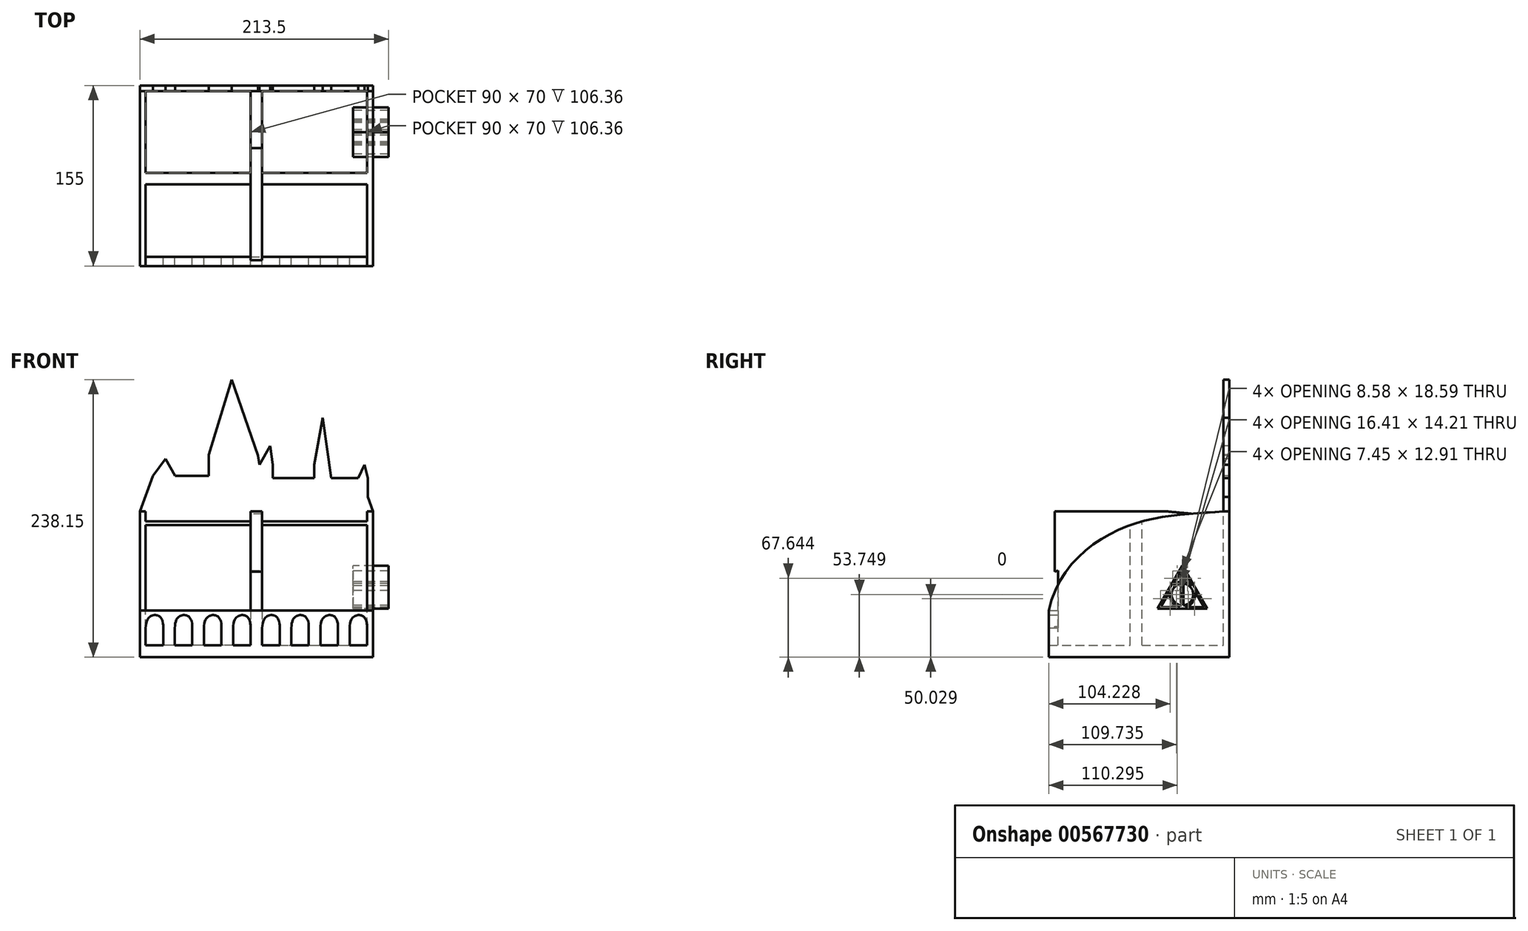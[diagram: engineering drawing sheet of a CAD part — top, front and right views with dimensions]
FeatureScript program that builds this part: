
annotation { "Feature Type Name" : "Feature", "Feature Type Description" : "" }
export const myFeature = defineFeature(function(context is Context, id is Id, definition is map)
    precondition{}
    {
        {
            var Q0;
            Q0=qCreatedBy(makeId("Front.planeOp"),FACE);
            var sketch = newSketch(context, id + "F0", { "sketchPlane" : qUnion([Q0])});
            skLineSegment(sketch, "E0", {"start": v(-120, -65.8) * mm, "end": v(80, -65.8) * mm});
            skLineSegment(sketch, "E1", {"start": v(-120, -65.8) * mm, "end": v(-120, -25.8) * mm});
            skLineSegment(sketch, "E2", {"start": v(80, -65.8) * mm, "end": v(80, -25.8) * mm});
            skLineSegment(sketch, "E3", {"start": v(-120, -25.8) * mm, "end": v(80, -25.8) * mm});
            skLineSegment(sketch, "E4", {"start": v(-115, -55.8) * mm, "end": v(-100, -55.8) * mm});
            skLineSegment(sketch, "E5", {"start": v(-90, -55.8) * mm, "end": v(-75, -55.8) * mm});
            skLineSegment(sketch, "E6", {"start": v(-65, -55.8) * mm, "end": v(-50, -55.8) * mm});
            skLineSegment(sketch, "E7", {"start": v(-40, -55.8) * mm, "end": v(-25, -55.8) * mm});
            skLineSegment(sketch, "E8", {"start": v(-15, -55.8) * mm, "end": v(0, -55.8) * mm});
            skLineSegment(sketch, "E9", {"start": v(10, -55.8) * mm, "end": v(25, -55.8) * mm});
            skLineSegment(sketch, "E10", {"start": v(35, -55.8) * mm, "end": v(50, -55.8) * mm});
            skLineSegment(sketch, "E11", {"start": v(60, -55.8) * mm, "end": v(75, -55.8) * mm});
            skLineSegment(sketch, "E12", {"start": v(-115, -55.8) * mm, "end": v(-115, -40.8) * mm});
            skLineSegment(sketch, "E13", {"start": v(-100, -55.8) * mm, "end": v(-100, -40.8) * mm});
            skLineSegment(sketch, "E14", {"start": v(-90, -55.8) * mm, "end": v(-90, -40.8) * mm});
            skLineSegment(sketch, "E15", {"start": v(-75, -55.8) * mm, "end": v(-75, -40.8) * mm});
            skLineSegment(sketch, "E16", {"start": v(-65, -55.8) * mm, "end": v(-65, -40.8) * mm});
            skLineSegment(sketch, "E17", {"start": v(-50, -55.8) * mm, "end": v(-50, -40.8) * mm});
            skLineSegment(sketch, "E18", {"start": v(-40, -55.8) * mm, "end": v(-40, -40.8) * mm});
            skLineSegment(sketch, "E19", {"start": v(-25, -55.8) * mm, "end": v(-25, -40.8) * mm});
            skLineSegment(sketch, "E20", {"start": v(-15, -55.8) * mm, "end": v(-15, -40.8) * mm});
            skLineSegment(sketch, "E21", {"start": v(0, -55.8) * mm, "end": v(0, -40.8) * mm});
            skLineSegment(sketch, "E22", {"start": v(10, -55.8) * mm, "end": v(10, -40.8) * mm});
            skLineSegment(sketch, "E23", {"start": v(25, -55.8) * mm, "end": v(25, -40.8) * mm});
            skLineSegment(sketch, "E24", {"start": v(35, -55.8) * mm, "end": v(35, -40.8) * mm});
            skLineSegment(sketch, "E25", {"start": v(50, -55.8) * mm, "end": v(50, -40.8) * mm});
            skLineSegment(sketch, "E26", {"start": v(60, -55.8) * mm, "end": v(60, -40.8) * mm});
            skLineSegment(sketch, "E27", {"start": v(75, -55.8) * mm, "end": v(75, -40.8) * mm});
            skFitSpline(sketch, "E28", {"points": [v(-115, -40.8) * mm, v(-107.07, -29.73) * mm, v(-100, -40.8) * mm], "startDerivative": vector(0.6, 51.8) * mm, "endDerivative": vector(-1.33, -52.67) * mm});
            skFitSpline(sketch, "E29", {"points": [v(-90, -40.8) * mm, v(-82.07, -29.73) * mm, v(-75, -40.8) * mm], "startDerivative": vector(0.6, 51.8) * mm, "endDerivative": vector(-1.33, -52.67) * mm});
            skFitSpline(sketch, "E30", {"points": [v(-65, -40.8) * mm, v(-57.07, -29.73) * mm, v(-50, -40.8) * mm], "startDerivative": vector(0.6, 51.8) * mm, "endDerivative": vector(-1.33, -52.67) * mm});
            skFitSpline(sketch, "E31", {"points": [v(-40, -40.8) * mm, v(-32.07, -29.73) * mm, v(-25, -40.8) * mm], "startDerivative": vector(0.6, 51.8) * mm, "endDerivative": vector(-1.33, -52.67) * mm});
            skFitSpline(sketch, "E32", {"points": [v(-15, -40.8) * mm, v(-7.07, -29.73) * mm, v(0, -40.8) * mm], "startDerivative": vector(0.6, 51.8) * mm, "endDerivative": vector(-1.33, -52.67) * mm});
            skFitSpline(sketch, "E33", {"points": [v(10, -40.8) * mm, v(17.93, -29.73) * mm, v(25, -40.8) * mm], "startDerivative": vector(0.6, 51.8) * mm, "endDerivative": vector(-1.33, -52.67) * mm});
            skFitSpline(sketch, "E34", {"points": [v(35, -40.8) * mm, v(42.93, -29.73) * mm, v(50, -40.8) * mm], "startDerivative": vector(0.6, 51.8) * mm, "endDerivative": vector(-1.33, -52.67) * mm});
            skFitSpline(sketch, "E35", {"points": [v(60, -40.8) * mm, v(67.93, -29.73) * mm, v(75, -40.8) * mm], "startDerivative": vector(0.6, 51.8) * mm, "endDerivative": vector(-1.33, -52.67) * mm});
            skSolve(sketch);
        }
        {
            var Q0;
            Q0=makeQuery(id+"F0.imprint","IMPRINT",FACE,{"disambiguationData":[TD([[makeQuery(id+"F0.imprint","IMPRINT",EDGE,{"derivedFrom":sQuery(id+"F0.wireOp",EDGE,"E0")}),1.0]])]});
            extrude(context, id + "F1", {"entities" : qUnion([Q0]), "depth" : 8 * mm, "offsetDistance" : 25 * mm});
        }
        {
            var Q0;
            Q0=makeQuery(id+"F1.opExtrude","SWEPT_FACE",FACE,{"disambiguationData":[OSD([sQuery(id+"F0.wireOp",EDGE,"E2")])]});
            var sketch = newSketch(context, id + "F2", { "sketchPlane" : qUnion([Q0])});
            skLineSegment(sketch, "E36", {"start": v(-8, -65.8) * mm, "end": v(142, -65.8) * mm});
            skLineSegment(sketch, "E37", {"start": v(142, -65.8) * mm, "end": v(142, 59.2) * mm});
            skFitSpline(sketch, "E38", {"points": [v(142, 59.2) * mm, v(58.95, 46.28) * mm, v(-8, -25.8) * mm], "startDerivative": vector(-167.04, -11.97) * mm, "endDerivative": vector(-46.18, -213.97) * mm});
            skSolve(sketch);
        }
        {
            var Q0;
            Q0=makeQuery(id+"F1.opExtrude","CAP_FACE",FACE,{"disambiguationData":[OSD([sQuery(id+"F0.wireOp",EDGE,"E0"),sQuery(id+"F0.wireOp",EDGE,"E1"),sQuery(id+"F0.wireOp",EDGE,"E2"),sQuery(id+"F0.wireOp",EDGE,"E3"),sQuery(id+"F0.wireOp",EDGE,"E4"),sQuery(id+"F0.wireOp",EDGE,"E5"),sQuery(id+"F0.wireOp",EDGE,"E6"),sQuery(id+"F0.wireOp",EDGE,"E7"),sQuery(id+"F0.wireOp",EDGE,"E8"),sQuery(id+"F0.wireOp",EDGE,"E9"),sQuery(id+"F0.wireOp",EDGE,"E10"),sQuery(id+"F0.wireOp",EDGE,"E11"),sQuery(id+"F0.wireOp",EDGE,"E12"),sQuery(id+"F0.wireOp",EDGE,"E13"),sQuery(id+"F0.wireOp",EDGE,"E14"),sQuery(id+"F0.wireOp",EDGE,"E15"),sQuery(id+"F0.wireOp",EDGE,"E16"),sQuery(id+"F0.wireOp",EDGE,"E17"),sQuery(id+"F0.wireOp",EDGE,"E18"),sQuery(id+"F0.wireOp",EDGE,"E19"),sQuery(id+"F0.wireOp",EDGE,"E20"),sQuery(id+"F0.wireOp",EDGE,"E21"),sQuery(id+"F0.wireOp",EDGE,"E22"),sQuery(id+"F0.wireOp",EDGE,"E23"),sQuery(id+"F0.wireOp",EDGE,"E24"),sQuery(id+"F0.wireOp",EDGE,"E25"),sQuery(id+"F0.wireOp",EDGE,"E26"),sQuery(id+"F0.wireOp",EDGE,"E27"),sQuery(id+"F0.wireOp",EDGE,"E28"),sQuery(id+"F0.wireOp",EDGE,"E29"),sQuery(id+"F0.wireOp",EDGE,"E30"),sQuery(id+"F0.wireOp",EDGE,"E31"),sQuery(id+"F0.wireOp",EDGE,"E32"),sQuery(id+"F0.wireOp",EDGE,"E33"),sQuery(id+"F0.wireOp",EDGE,"E34"),sQuery(id+"F0.wireOp",EDGE,"E35")])],"isStart":true});
            cPlane(context, id + "F3", {"entities" : qUnion([Q0]), "cplaneType" : CPlaneType.OFFSET, "offset" : 142 * mm, "width" : 150 * mm, "height" : 150 * mm});
        }
        {
            var Q0;
            Q0=qCreatedBy(id+"F3.planeOp",FACE);
            var sketch = newSketch(context, id + "F4", { "sketchPlane" : qUnion([Q0])});
            skPoint(sketch, "E39.0", {"position": v(-80, 59.2) * mm});
            skPoint(sketch, "E40.0", {"position": v(-80, -65.8) * mm});
            skPoint(sketch, "E41", {"position": v(120, 59.2) * mm});
            skPoint(sketch, "E42", {"position": v(120, -65.8) * mm});
            skLineSegment(sketch, "E43", {"start": v(-80, 59.2) * mm, "end": v(-80, -65.8) * mm});
            skLineSegment(sketch, "E44", {"start": v(-80, -65.8) * mm, "end": v(120, -65.8) * mm});
            skLineSegment(sketch, "E45", {"start": v(120, -65.8) * mm, "end": v(120, 59.2) * mm});
            skLineSegment(sketch, "E46", {"start": v(-80, 59.2) * mm, "end": v(-75.6, 71.64) * mm});
            skLineSegment(sketch, "E47", {"start": v(-75.6, 71.64) * mm, "end": v(-75.6, 87.92) * mm});
            skLineSegment(sketch, "E48", {"start": v(-75.6, 87.92) * mm, "end": v(-72.68, 99.19) * mm});
            skLineSegment(sketch, "E49", {"start": v(-72.68, 99.19) * mm, "end": v(-67.26, 87.92) * mm});
            skLineSegment(sketch, "E50", {"start": v(-67.26, 87.92) * mm, "end": v(-44.24, 87.92) * mm});
            skLineSegment(sketch, "E51", {"start": v(-44.24, 87.92) * mm, "end": v(-36.93, 139.5) * mm});
            skLineSegment(sketch, "E52", {"start": v(-36.93, 139.5) * mm, "end": v(-29.61, 99.19) * mm});
            skLineSegment(sketch, "E53", {"start": v(-29.61, 99.19) * mm, "end": v(-29.61, 87.92) * mm});
            skLineSegment(sketch, "E54", {"start": v(-29.61, 87.92) * mm, "end": v(5.9, 87.92) * mm});
            skLineSegment(sketch, "E55", {"start": v(5.9, 87.92) * mm, "end": v(5.9, 99.19) * mm});
            skLineSegment(sketch, "E56", {"start": v(5.9, 99.19) * mm, "end": v(8.21, 115.44) * mm});
            skLineSegment(sketch, "E57", {"start": v(8.21, 115.44) * mm, "end": v(17.42, 99.19) * mm});
            skLineSegment(sketch, "E58", {"start": v(17.42, 99.19) * mm, "end": v(18.57, 107.31) * mm});
            skPoint(sketch, "E58.endSnap0", {"position": v(12.82, 107.31) * mm});
            skLineSegment(sketch, "E59", {"start": v(18.57, 107.31) * mm, "end": v(41.03, 172.35) * mm});
            skLineSegment(sketch, "E60", {"start": v(41.03, 172.35) * mm, "end": v(60.84, 107.7) * mm});
            skLineSegment(sketch, "E61", {"start": v(60.84, 107.7) * mm, "end": v(60.84, 89.66) * mm});
            skLineSegment(sketch, "E62", {"start": v(60.84, 89.66) * mm, "end": v(89.78, 89.66) * mm});
            skLineSegment(sketch, "E63", {"start": v(89.78, 89.66) * mm, "end": v(98.17, 104.34) * mm});
            skLineSegment(sketch, "E64", {"start": v(98.17, 104.34) * mm, "end": v(108.65, 89.66) * mm});
            skLineSegment(sketch, "E65", {"start": v(108.65, 89.66) * mm, "end": v(120, 59.2) * mm});
            skSolve(sketch);
        }
        {
            var Q0;
            Q0=makeQuery(id+"F1.opExtrude","SWEPT_FACE",FACE,{"disambiguationData":[OSD([sQuery(id+"F0.wireOp",EDGE,"E1")])]});
            var sketch = newSketch(context, id + "F5", { "sketchPlane" : qUnion([Q0])});
            skPoint(sketch, "E66.0", {"position": v(-142, 59.2) * mm});
            skPoint(sketch, "E67.0", {"position": v(-142, -65.8) * mm});
            skLineSegment(sketch, "E68", {"start": v(-142, 59.2) * mm, "end": v(-142, -65.8) * mm});
            skLineSegment(sketch, "E69", {"start": v(-142, -65.8) * mm, "end": v(0, -65.8) * mm});
            skLineSegment(sketch, "E70", {"start": v(0, -65.8) * mm, "end": v(0, -25.8) * mm});
            skLineSegment(sketch, "E71", {"start": v(0, -25.8) * mm, "end": v(8, -25.8) * mm});
            skFitSpline(sketch, "E72.MirrorCS", {"points": [v(-142, 59.2) * mm, v(-58.95, 46.28) * mm, v(8, -25.8) * mm], "startDerivative": vector(167.04, -11.97) * mm, "endDerivative": vector(46.18, -213.97) * mm});
            skSolve(sketch);
        }
        {
            var Q0;
            Q0=makeQuery(id+"F1.opExtrude","SWEPT_FACE",FACE,{"disambiguationData":[OSD([sQuery(id+"F0.wireOp",EDGE,"E0")])]});
            var sketch = newSketch(context, id + "F6", { "sketchPlane" : qUnion([Q0])});
            skPoint(sketch, "E73.0", {"position": v(-120, 8) * mm});
            skPoint(sketch, "E74.0", {"position": v(-120, -142) * mm});
            skPoint(sketch, "E75.0", {"position": v(80, -142) * mm});
            skPoint(sketch, "E76.0", {"position": v(80, 8) * mm});
            skLineSegment(sketch, "E77.bottom", {"start": v(-120, 8) * mm, "end": v(80, 8) * mm});
            skLineSegment(sketch, "E77.top", {"start": v(-120, -142) * mm, "end": v(80, -142) * mm});
            skLineSegment(sketch, "E77.left", {"start": v(-120, 8) * mm, "end": v(-120, -142) * mm});
            skLineSegment(sketch, "E77.right", {"start": v(80, 8) * mm, "end": v(80, -142) * mm});
            skSolve(sketch);
        }
        {
            var Q0;
            {var subQ0=sQuery(id+"F6.wireOp",EDGE,"E77.top");Q0=makeQuery(id+"F6.imprint","IMPRINT",FACE,{"disambiguationData":[TD([[makeQuery(id+"F6.imprint","IMPRINT",EDGE,{"derivedFrom":subQ0}),1.0]])]});}
            extrude(context, id + "F7", {"entities" : qUnion([Q0]), "operationType" : NewBodyOperationType.ADD, "oppositeDirection" : true, "depth" : 10 * mm, "offsetDistance" : 25 * mm});
        }
        {
            var Q0;
            {var subQ1=sQuery(id+"F2.wireOp",EDGE,"E37");Q0=makeQuery(id+"F2.imprint","IMPRINT",FACE,{"disambiguationData":[TD([[makeQuery(id+"F2.imprint","IMPRINT",EDGE,{"derivedFrom":subQ1}),1.0]])]});}
            extrude(context, id + "F8", {"entities" : qUnion([Q0]), "operationType" : NewBodyOperationType.ADD, "oppositeDirection" : true, "depth" : 5 * mm, "offsetDistance" : 25 * mm});
        }
        {
            var Q0;
            Q0=makeQuery(id+"F5.imprint","IMPRINT",FACE,{"disambiguationData":[TD([[makeQuery(id+"F5.imprint","IMPRINT",EDGE,{"derivedFrom":sQuery(id+"F5.wireOp",EDGE,"E68")}),1.0]])]});
            extrude(context, id + "F9", {"entities" : qUnion([Q0]), "operationType" : NewBodyOperationType.ADD, "oppositeDirection" : true, "depth" : 5 * mm, "offsetDistance" : 25 * mm});
        }
        {
            var Q0;
            Q0=makeQuery(id+"F4.imprint","IMPRINT",FACE,{"disambiguationData":[TD([[makeQuery(id+"F4.imprint","IMPRINT",EDGE,{"derivedFrom":sQuery(id+"F4.wireOp",EDGE,"E43")}),1.0]])]});
            extrude(context, id + "F10", {"entities" : qUnion([Q0]), "operationType" : NewBodyOperationType.ADD, "depth" : 5 * mm, "offsetDistance" : 25 * mm});
        }
        {
            var Q0;
            Q0=makeQuery(id+"F10.opExtrude","CAP_FACE",FACE,{"disambiguationData":[OSD([sQuery(id+"F4.wireOp",EDGE,"E43"),sQuery(id+"F4.wireOp",EDGE,"E44"),sQuery(id+"F4.wireOp",EDGE,"E45"),sQuery(id+"F4.wireOp",EDGE,"E46"),sQuery(id+"F4.wireOp",EDGE,"E47"),sQuery(id+"F4.wireOp",EDGE,"E48"),sQuery(id+"F4.wireOp",EDGE,"E49"),sQuery(id+"F4.wireOp",EDGE,"E50"),sQuery(id+"F4.wireOp",EDGE,"E51"),sQuery(id+"F4.wireOp",EDGE,"E52"),sQuery(id+"F4.wireOp",EDGE,"E53"),sQuery(id+"F4.wireOp",EDGE,"E54"),sQuery(id+"F4.wireOp",EDGE,"E55"),sQuery(id+"F4.wireOp",EDGE,"E56"),sQuery(id+"F4.wireOp",EDGE,"E57"),sQuery(id+"F4.wireOp",EDGE,"E58"),sQuery(id+"F4.wireOp",EDGE,"E59"),sQuery(id+"F4.wireOp",EDGE,"E60"),sQuery(id+"F4.wireOp",EDGE,"E61"),sQuery(id+"F4.wireOp",EDGE,"E62"),sQuery(id+"F4.wireOp",EDGE,"E63"),sQuery(id+"F4.wireOp",EDGE,"E64"),sQuery(id+"F4.wireOp",EDGE,"E65")])],"isStart":true});
            var sketch = newSketch(context, id + "F11", { "sketchPlane" : qUnion([Q0])});
            skLineSegment(sketch, "E78", {"start": v(-115, -55.8) * mm, "end": v(-25, -55.8) * mm});
            skLineSegment(sketch, "E79.bottom", {"start": v(-25, -55.8) * mm, "end": v(-15, -55.8) * mm});
            skLineSegment(sketch, "E79.top", {"start": v(-25, 59.2) * mm, "end": v(-15, 59.2) * mm});
            skLineSegment(sketch, "E79.left", {"start": v(-25, -55.8) * mm, "end": v(-25, 59.2) * mm});
            skLineSegment(sketch, "E79.right", {"start": v(-15, -55.8) * mm, "end": v(-15, 59.2) * mm});
            skSolve(sketch);
        }
        {
            var Q0;
            Q0=makeQuery(id+"F9.boolean.opBoolean","MERGE",FACE,{"derivedFrom":[makeQuery(id+"F1.opExtrude","SWEPT_FACE",FACE,{"disambiguationData":[OSD([sQuery(id+"F0.wireOp",EDGE,"E12")])]}),makeQuery(id+"F9.opExtrude","CAP_FACE",FACE,{"disambiguationData":[OSD([sQuery(id+"F5.wireOp",EDGE,"E68"),sQuery(id+"F5.wireOp",EDGE,"E69"),sQuery(id+"F5.wireOp",EDGE,"E70"),sQuery(id+"F5.wireOp",EDGE,"E71"),sQuery(id+"F5.wireOp",EDGE,"E72.MirrorCS")])],"isStart":false})]});
            var sketch = newSketch(context, id + "F12", { "sketchPlane" : qUnion([Q0])});
            skLineSegment(sketch, "E80", {"start": v(-8, -55.8) * mm, "end": v(62, -55.8) * mm});
            skLineSegment(sketch, "E81.bottom", {"start": v(62, -55.8) * mm, "end": v(72, -55.8) * mm});
            skLineSegment(sketch, "E81.top", {"start": v(62, 90.16) * mm, "end": v(72, 90.16) * mm});
            skLineSegment(sketch, "E81.left", {"start": v(62, -55.8) * mm, "end": v(62, 90.16) * mm});
            skLineSegment(sketch, "E81.right", {"start": v(72, -55.8) * mm, "end": v(72, 90.16) * mm});
            skSolve(sketch);
        }
        {
            var Q0;
            {var subQ0=sQuery(id+"F12.wireOp",EDGE,"E81.bottom");Q0=makeQuery(id+"F12.imprint","IMPRINT",FACE,{"disambiguationData":[TD([[makeQuery(id+"F12.imprint","IMPRINT",EDGE,{"derivedFrom":subQ0}),1.0]])]});}
            extrude(context, id + "F13", {"entities" : qUnion([Q0]), "operationType" : NewBodyOperationType.ADD, "depth" : 90 * mm, "offsetDistance" : 25 * mm});
        }
        {
            var Q0;
            Q0=makeQuery(id+"F8.boolean.opBoolean","MERGE",FACE,{"derivedFrom":[makeQuery(id+"F1.opExtrude","SWEPT_FACE",FACE,{"disambiguationData":[OSD([sQuery(id+"F0.wireOp",EDGE,"E27")])]}),makeQuery(id+"F8.opExtrude","CAP_FACE",FACE,{"disambiguationData":[OSD([sQuery(id+"F0.wireOp",EDGE,"E2"),sQuery(id+"F0.wireOp",EDGE,"E3"),sQuery(id+"F2.wireOp",EDGE,"E36"),sQuery(id+"F2.wireOp",EDGE,"E37"),sQuery(id+"F2.wireOp",EDGE,"E38")])],"isStart":false})]});
            var sketch = newSketch(context, id + "F14", { "sketchPlane" : qUnion([Q0])});
            skLineSegment(sketch, "E82", {"start": v(-142, -55.8) * mm, "end": v(-72, -55.8) * mm});
            skLineSegment(sketch, "E83.bottom", {"start": v(-72, -55.8) * mm, "end": v(-62, -55.8) * mm});
            skLineSegment(sketch, "E83.top", {"start": v(-72, 77.76) * mm, "end": v(-62, 77.76) * mm});
            skLineSegment(sketch, "E83.left", {"start": v(-72, -55.8) * mm, "end": v(-72, 77.76) * mm});
            skLineSegment(sketch, "E83.right", {"start": v(-62, -55.8) * mm, "end": v(-62, 77.76) * mm});
            skSolve(sketch);
        }
        {
            var Q0;
            {var subQ0=sQuery(id+"F14.wireOp",EDGE,"E83.bottom");Q0=makeQuery(id+"F14.imprint","IMPRINT",FACE,{"disambiguationData":[TD([[makeQuery(id+"F14.imprint","IMPRINT",EDGE,{"derivedFrom":subQ0}),-1.0]])]});}
            extrude(context, id + "F15", {"entities" : qUnion([Q0]), "operationType" : NewBodyOperationType.ADD, "depth" : 90 * mm, "offsetDistance" : 25 * mm});
        }
        {
            var Q0;
            Q0=makeQuery(id+"F11.imprint","IMPRINT",FACE,{"disambiguationData":[TD([[makeQuery(id+"F11.imprint","IMPRINT",EDGE,{"derivedFrom":sQuery(id+"F11.wireOp",EDGE,"E79.bottom")}),1.0]])]});
            extrude(context, id + "F16", {"entities" : qUnion([Q0]), "operationType" : NewBodyOperationType.ADD, "depth" : 145 * mm, "offsetDistance" : 25 * mm});
        }
        {
            var Q0;
            Q0=makeQuery(id+"F16.boolean.opBoolean","MERGE",FACE,{"derivedFrom":[makeQuery(id+"F1.opExtrude","SWEPT_FACE",FACE,{"disambiguationData":[OSD([sQuery(id+"F0.wireOp",EDGE,"E20")])]}),makeQuery(id+"F16.opExtrude","SWEPT_FACE",FACE,{"disambiguationData":[OSD([sQuery(id+"F11.wireOp",EDGE,"E79.right")])]})]});
            var sketch = newSketch(context, id + "F17", { "sketchPlane" : qUnion([Q0])});
            skFitSpline(sketch, "E84.0", {"points": [v(142, 59.2) * mm, v(115.26, 57.28) * mm, v(55.74, 56.51) * mm, v(0, 11.26) * mm, v(-8, -25.8) * mm]});
            skLineSegment(sketch, "E85.0", {"start": v(-3, 59.2) * mm, "end": v(142, 59.2) * mm});
            skLineSegment(sketch, "E86", {"start": v(-3, 59.2) * mm, "end": v(-3, -9.9) * mm});
            skSolve(sketch);
        }
        {
            var Q0;
            {var subQ0=sQuery(id+"F17.wireOp",EDGE,"E85.0");Q0=makeQuery(id+"F17.imprint","IMPRINT",FACE,{"disambiguationData":[TD([[makeQuery(id+"F17.imprint","IMPRINT",EDGE,{"derivedFrom":subQ0}),-1.0]])]});}
            extrude(context, id + "F18", {"entities" : qUnion([Q0]), "operationType" : NewBodyOperationType.REMOVE, "oppositeDirection" : true, "depth" : 51 * mm, "offsetDistance" : 25 * mm});
        }
        {
            var Q0;
            {var subQ22=sQuery(id+"F0.wireOp",EDGE,"E20");var subQ33=sQuery(id+"F0.wireOp",EDGE,"E3");var subQ37=sQuery(id+"F11.wireOp",EDGE,"E79.right");Q0=makeQuery(id+"F18.boolean.opBoolean","SPLIT",FACE,{"disambiguationData":[TD([makeQuery(id+"F1.opExtrude","SWEPT_FACE",FACE,{"disambiguationData":[OSD([subQ33])]})])],"derivedFrom":makeQuery(id+"F16.boolean.opBoolean","MERGE",FACE,{"derivedFrom":[makeQuery(id+"F1.opExtrude","SWEPT_FACE",FACE,{"disambiguationData":[OSD([subQ22])]}),makeQuery(id+"F16.opExtrude","SWEPT_FACE",FACE,{"disambiguationData":[OSD([subQ37])]})]})});}
            var sketch = newSketch(context, id + "F19", { "sketchPlane" : qUnion([Q0])});
            skLineSegment(sketch, "E87", {"start": v(0, -25.8) * mm, "end": v(-3, -25.8) * mm});
            skLineSegment(sketch, "E88", {"start": v(-3, -25.8) * mm, "end": v(-3, -9.9) * mm});
            skLineSegment(sketch, "E89", {"start": v(0, -25.8) * mm, "end": v(0, 8.53) * mm});
            skLineSegment(sketch, "E90", {"start": v(0, 8.53) * mm, "end": v(-3, 7.58) * mm});
            skLineSegment(sketch, "E91", {"start": v(-3, 7.58) * mm, "end": v(-3, -9.9) * mm});
            skSolve(sketch);
        }
        {
            var Q0;
            {var subQ0=sQuery(id+"F19.wireOp",EDGE,"E87");Q0=makeQuery(id+"F19.imprint","IMPRINT",FACE,{"disambiguationData":[TD([[makeQuery(id+"F19.imprint","IMPRINT",EDGE,{"derivedFrom":subQ0}),-1.0]])]});}
            extrude(context, id + "F20", {"entities" : qUnion([Q0]), "operationType" : NewBodyOperationType.REMOVE, "oppositeDirection" : true, "depth" : 25 * mm, "offsetDistance" : 25 * mm});
        }
        {
            var Q0;
            {var subQ0=sQuery(id+"F0.wireOp",EDGE,"E2");Q0=makeQuery(id+"F10.boolean.opBoolean","MERGE",FACE,{"derivedFrom":[makeQuery(id+"F8.boolean.opBoolean","MERGE",FACE,{"derivedFrom":[makeQuery(id+"F7.boolean.opBoolean","MERGE",FACE,{"derivedFrom":[makeQuery(id+"F1.opExtrude","SWEPT_FACE",FACE,{"disambiguationData":[OSD([subQ0])]}),makeQuery(id+"F7.opExtrude","SWEPT_FACE",FACE,{"disambiguationData":[OSD([sQuery(id+"F6.wireOp",EDGE,"E77.right")])]})]}),makeQuery(id+"F8.opExtrude","CAP_FACE",FACE,{"disambiguationData":[OSD([subQ0,sQuery(id+"F0.wireOp",EDGE,"E3"),sQuery(id+"F2.wireOp",EDGE,"E36"),sQuery(id+"F2.wireOp",EDGE,"E37"),sQuery(id+"F2.wireOp",EDGE,"E38")])],"isStart":true})]}),makeQuery(id+"F10.opExtrude","SWEPT_FACE",FACE,{"disambiguationData":[OSD([sQuery(id+"F4.wireOp",EDGE,"E43")])]})]});}
            cPlane(context, id + "F21", {"entities" : qUnion([Q0]), "cplaneType" : CPlaneType.OFFSET, "offset" : 0 * mm, "width" : 150 * mm, "height" : 150 * mm});
        }
        {
            var Q0;
            Q0=qCreatedBy(id+"F21.planeOp",FACE);
            var sketch = newSketch(context, id + "F22", { "sketchPlane" : qUnion([Q0])});
            skLineSegment(sketch, "E92", {"start": v(28.04, -45.75) * mm, "end": v(44.45, -17.33) * mm});
            skLineSegment(sketch, "E93", {"start": v(67.04, 16.6) * mm, "end": v(81.95, -9.22) * mm});
            skLineSegment(sketch, "E94", {"start": v(28.04, -45.75) * mm, "end": v(60.86, -45.75) * mm});
            skPoint(sketch, "E95.0", {"position": v(69.5, -65.8) * mm});
            skLineSegment(sketch, "E96.0", {"start": v(22.85, -48.75) * mm, "end": v(65.54, 25.2) * mm});
            skLineSegment(sketch, "E96.1", {"start": v(22.85, -48.75) * mm, "end": v(108.24, -48.75) * mm});
            skLineSegment(sketch, "E96.2", {"start": v(65.54, 25.2) * mm, "end": v(108.24, -48.75) * mm});
            skLineSegment(sketch, "E97.left", {"start": v(64.04, 16.6) * mm, "end": v(64.04, -2) * mm});
            skLineSegment(sketch, "E97.right", {"start": v(67.04, 16.6) * mm, "end": v(67.04, -2) * mm});
            skPoint(sketch, "E97.middle", {"position": v(65.54, -13.28) * mm});
            skArc(sketch, "E98.0", {"start": v(64.04, -5.51) * mm, "mid": v(46.9, -24.1) * mm, "end": v(64.04, -42.7) * mm});
            skLineSegment(sketch, "E99.trimOffspring", {"start": v(64.04, -5.51) * mm, "end": v(64.04, -42.7) * mm});
            skLineSegment(sketch, "E100.trimOffspring", {"start": v(67.04, -5.51) * mm, "end": v(67.04, -42.7) * mm});
            skPoint(sketch, "E101.orphan", {"position": v(64.04, 19.2) * mm});
            skPoint(sketch, "E102.orphan", {"position": v(67.04, 19.2) * mm});
            skPoint(sketch, "E103.orphan", {"position": v(65.54, 19.2) * mm});
            skArc(sketch, "E104.trimOffspring", {"start": v(67.04, -42.7) * mm, "mid": v(84.2, -24.1) * mm, "end": v(67.04, -5.51) * mm});
            skLineSegment(sketch, "E105.trimOffspring", {"start": v(70.22, -45.75) * mm, "end": v(103.04, -45.75) * mm});
            skLineSegment(sketch, "E106.trimOffspring", {"start": v(64.04, -45.7) * mm, "end": v(64.04, -45.75) * mm});
            skLineSegment(sketch, "E107.trimOffspring", {"start": v(67.04, -45.7) * mm, "end": v(67.04, -45.75) * mm});
            skArc(sketch, "E108.0", {"start": v(70.22, -45.75) * mm, "mid": v(84.73, -35.18) * mm, "end": v(86.63, -17.33) * mm});
            skArc(sketch, "E109.0", {"start": v(64.01, -2) * mm, "mid": v(55.87, -4.17) * mm, "end": v(49.13, -9.22) * mm});
            skLineSegment(sketch, "E110.trimOffspring", {"start": v(49.13, -9.22) * mm, "end": v(64.04, 16.6) * mm});
            skArc(sketch, "E111.trimOffspring", {"start": v(44.45, -17.33) * mm, "mid": v(46.36, -35.18) * mm, "end": v(60.86, -45.75) * mm});
            skLineSegment(sketch, "E112", {"start": v(64.01, -2) * mm, "end": v(64.04, -2) * mm});
            skLineSegment(sketch, "E113", {"start": v(67.08, -2) * mm, "end": v(67.04, -2) * mm});
            skArc(sketch, "E114.trimOffspring", {"start": v(81.95, -9.22) * mm, "mid": v(75.22, -4.17) * mm, "end": v(67.08, -2) * mm});
            skLineSegment(sketch, "E115.trimOffspring", {"start": v(86.63, -17.33) * mm, "end": v(103.04, -45.75) * mm});
            skSolve(sketch);
        }
        {
            var Q0;
            Q0 = qSketchRegion(id + "F22", true);
            extrude(context, id + "F23", {"entities" : qUnion([Q0]), "depth" : 61 * mm, "offsetDistance" : 25 * mm});
        }
        {
            var Q0;
            Q0=makeQuery(id+"F23.opExtrude","SWEPT_BODY",BODY,{"disambiguationData":[OSD([sQuery(id+"F22.wireOp",EDGE,"E92"),sQuery(id+"F22.wireOp",EDGE,"E93"),sQuery(id+"F22.wireOp",EDGE,"E94"),sQuery(id+"F22.wireOp",EDGE,"E96.0"),sQuery(id+"F22.wireOp",EDGE,"E96.1"),sQuery(id+"F22.wireOp",EDGE,"E96.2"),sQuery(id+"F22.wireOp",EDGE,"E97.left"),sQuery(id+"F22.wireOp",EDGE,"E97.right"),sQuery(id+"F22.wireOp",EDGE,"E98.0"),sQuery(id+"F22.wireOp",EDGE,"E99.trimOffspring"),sQuery(id+"F22.wireOp",EDGE,"E100.trimOffspring"),sQuery(id+"F22.wireOp",EDGE,"E104.trimOffspring"),sQuery(id+"F22.wireOp",EDGE,"E105.trimOffspring"),sQuery(id+"F22.wireOp",EDGE,"E108.0"),sQuery(id+"F22.wireOp",EDGE,"E109.0"),sQuery(id+"F22.wireOp",EDGE,"E110.trimOffspring"),sQuery(id+"F22.wireOp",EDGE,"E111.trimOffspring"),sQuery(id+"F22.wireOp",EDGE,"E112"),sQuery(id+"F22.wireOp",EDGE,"E113"),sQuery(id+"F22.wireOp",EDGE,"E114.trimOffspring"),sQuery(id+"F22.wireOp",EDGE,"E115.trimOffspring")])]});
            var Q1;
            Q1=qCreatedBy(makeId("Origin.pointOp"),VERTEX);
            transform(context, id + "F24", {"entities" : qUnion([Q0]), "transformType" : TransformType.SCALE_UNIFORMLY, "scale" : 0.5, "scalePoint" : qUnion([Q1]), "makeCopy" : false});
        }
        {
            var Q0;
            Q0=makeQuery(id+"F23.opExtrude","SWEPT_BODY",BODY,{"disambiguationData":[OSD([sQuery(id+"F22.wireOp",EDGE,"E92"),sQuery(id+"F22.wireOp",EDGE,"E93"),sQuery(id+"F22.wireOp",EDGE,"E94"),sQuery(id+"F22.wireOp",EDGE,"E96.0"),sQuery(id+"F22.wireOp",EDGE,"E96.1"),sQuery(id+"F22.wireOp",EDGE,"E96.2"),sQuery(id+"F22.wireOp",EDGE,"E97.left"),sQuery(id+"F22.wireOp",EDGE,"E97.right"),sQuery(id+"F22.wireOp",EDGE,"E98.0"),sQuery(id+"F22.wireOp",EDGE,"E99.trimOffspring"),sQuery(id+"F22.wireOp",EDGE,"E100.trimOffspring"),sQuery(id+"F22.wireOp",EDGE,"E104.trimOffspring"),sQuery(id+"F22.wireOp",EDGE,"E105.trimOffspring"),sQuery(id+"F22.wireOp",EDGE,"E108.0"),sQuery(id+"F22.wireOp",EDGE,"E109.0"),sQuery(id+"F22.wireOp",EDGE,"E110.trimOffspring"),sQuery(id+"F22.wireOp",EDGE,"E111.trimOffspring"),sQuery(id+"F22.wireOp",EDGE,"E112"),sQuery(id+"F22.wireOp",EDGE,"E113"),sQuery(id+"F22.wireOp",EDGE,"E114.trimOffspring"),sQuery(id+"F22.wireOp",EDGE,"E115.trimOffspring")])]});
            transform(context, id + "F25", {"entities" : qUnion([Q0]), "transformType" : TransformType.TRANSLATION_3D, "dx" : 23 * mm, "dy" : 74 * mm, "dz" : 0 * mm, "makeCopy" : false});
        }
        {
            var Q0;
            {var subQ0=sQuery(id+"F0.wireOp",EDGE,"E2");Q0=makeQuery(id+"F10.boolean.opBoolean","MERGE",FACE,{"derivedFrom":[makeQuery(id+"F8.boolean.opBoolean","MERGE",FACE,{"derivedFrom":[makeQuery(id+"F7.boolean.opBoolean","MERGE",FACE,{"derivedFrom":[makeQuery(id+"F1.opExtrude","SWEPT_FACE",FACE,{"disambiguationData":[OSD([subQ0])]}),makeQuery(id+"F7.opExtrude","SWEPT_FACE",FACE,{"disambiguationData":[OSD([sQuery(id+"F6.wireOp",EDGE,"E77.right")])]})]}),makeQuery(id+"F8.opExtrude","CAP_FACE",FACE,{"disambiguationData":[OSD([subQ0,sQuery(id+"F0.wireOp",EDGE,"E3"),sQuery(id+"F2.wireOp",EDGE,"E36"),sQuery(id+"F2.wireOp",EDGE,"E37"),sQuery(id+"F2.wireOp",EDGE,"E38")])],"isStart":true})]}),makeQuery(id+"F10.opExtrude","SWEPT_FACE",FACE,{"disambiguationData":[OSD([sQuery(id+"F4.wireOp",EDGE,"E43")])]})]});}
            cPlane(context, id + "F26", {"entities" : qUnion([Q0]), "cplaneType" : CPlaneType.OFFSET, "offset" : 0 * mm, "width" : 150 * mm, "height" : 150 * mm});
        }
        {
            var Q0;
            Q0=qCreatedBy(id+"F26.planeOp",FACE);
            var sketch = newSketch(context, id + "F27", { "sketchPlane" : qUnion([Q0])});
            skLineSegment(sketch, "E116.0.0", {"start": v(128.12, -24.38) * mm, "end": v(106.77, 12.6) * mm});
            skLineSegment(sketch, "E116.0.1", {"start": v(106.77, 12.6) * mm, "end": v(85.42, -24.38) * mm});
            skLineSegment(sketch, "E116.0.2", {"start": v(85.42, -24.38) * mm, "end": v(128.12, -24.38) * mm});
            skLineSegment(sketch, "E117.0", {"start": v(98.57, -4.61) * mm, "end": v(106.02, 8.3) * mm});
            skArc(sketch, "E118.0", {"start": v(106, -1) * mm, "mid": v(101.94, -2.09) * mm, "end": v(98.57, -4.61) * mm});
            skLineSegment(sketch, "E119.0", {"start": v(106.02, 8.3) * mm, "end": v(106.02, -1) * mm});
            skArc(sketch, "E120.0", {"start": v(114.98, -4.61) * mm, "mid": v(111.6, -2.09) * mm, "end": v(107.54, -1) * mm});
            skLineSegment(sketch, "E121.0", {"start": v(107.52, 8.3) * mm, "end": v(107.52, -1) * mm});
            skLineSegment(sketch, "E122.0", {"start": v(107.52, 8.3) * mm, "end": v(114.98, -4.61) * mm});
            skArc(sketch, "E123.0", {"start": v(107.52, -21.35) * mm, "mid": v(116.1, -12.05) * mm, "end": v(107.52, -2.76) * mm});
            skLineSegment(sketch, "E124.0", {"start": v(107.52, -2.76) * mm, "end": v(107.52, -21.35) * mm});
            skLineSegment(sketch, "E125.0", {"start": v(106.02, -2.76) * mm, "end": v(106.02, -21.35) * mm});
            skArc(sketch, "E126.0", {"start": v(106.02, -2.76) * mm, "mid": v(97.45, -12.05) * mm, "end": v(106.02, -21.35) * mm});
            skLineSegment(sketch, "E127.0", {"start": v(109.11, -22.88) * mm, "end": v(125.52, -22.88) * mm});
            skLineSegment(sketch, "E128.0", {"start": v(117.32, -8.66) * mm, "end": v(125.52, -22.88) * mm});
            skArc(sketch, "E129.0", {"start": v(109.11, -22.88) * mm, "mid": v(116.36, -17.59) * mm, "end": v(117.32, -8.66) * mm});
            skLineSegment(sketch, "E130.0", {"start": v(88.02, -22.88) * mm, "end": v(104.43, -22.88) * mm});
            skArc(sketch, "E131.0", {"start": v(96.23, -8.66) * mm, "mid": v(97.18, -17.59) * mm, "end": v(104.43, -22.88) * mm});
            skLineSegment(sketch, "E132.0", {"start": v(88.02, -22.88) * mm, "end": v(96.23, -8.66) * mm});
            skLineSegment(sketch, "E133", {"start": v(106, -1) * mm, "end": v(106.02, -1) * mm});
            skLineSegment(sketch, "E134", {"start": v(107.52, -1) * mm, "end": v(107.54, -1) * mm});
            skSolve(sketch);
        }
        {
            var Q0;
            Q0=makeQuery(id+"F27.imprint","IMPRINT",FACE,{"disambiguationData":[TD([[makeQuery(id+"F27.imprint","IMPRINT",EDGE,{"derivedFrom":sQuery(id+"F27.wireOp",EDGE,"E130.0")}),1.0]])]});
            var Q1;
            Q1=makeQuery(id+"F27.imprint","IMPRINT",FACE,{"disambiguationData":[TD([[makeQuery(id+"F27.imprint","IMPRINT",EDGE,{"derivedFrom":sQuery(id+"F27.wireOp",EDGE,"E125.0")}),-1.0]])]});
            var Q2;
            Q2=makeQuery(id+"F27.imprint","IMPRINT",FACE,{"disambiguationData":[TD([[makeQuery(id+"F27.imprint","IMPRINT",EDGE,{"derivedFrom":sQuery(id+"F27.wireOp",EDGE,"E123.0")}),1.0]])]});
            var Q3;
            Q3=makeQuery(id+"F27.imprint","IMPRINT",FACE,{"disambiguationData":[TD([[makeQuery(id+"F27.imprint","IMPRINT",EDGE,{"derivedFrom":sQuery(id+"F27.wireOp",EDGE,"E120.0")}),-1.0]])]});
            var Q4;
            Q4=makeQuery(id+"F27.imprint","IMPRINT",FACE,{"disambiguationData":[TD([[makeQuery(id+"F27.imprint","IMPRINT",EDGE,{"derivedFrom":sQuery(id+"F27.wireOp",EDGE,"E117.0")}),-1.0]])]});
            var Q5;
            Q5=makeQuery(id+"F27.imprint","IMPRINT",FACE,{"disambiguationData":[TD([[makeQuery(id+"F27.imprint","IMPRINT",EDGE,{"derivedFrom":sQuery(id+"F27.wireOp",EDGE,"E127.0")}),1.0]])]});
            extrude(context, id + "F28", {"entities" : qUnion([Q0, Q1, Q2, Q3, Q4, Q5]), "operationType" : NewBodyOperationType.REMOVE, "oppositeDirection" : true, "depth" : 25 * mm, "offsetDistance" : 25 * mm});
        }
    });
